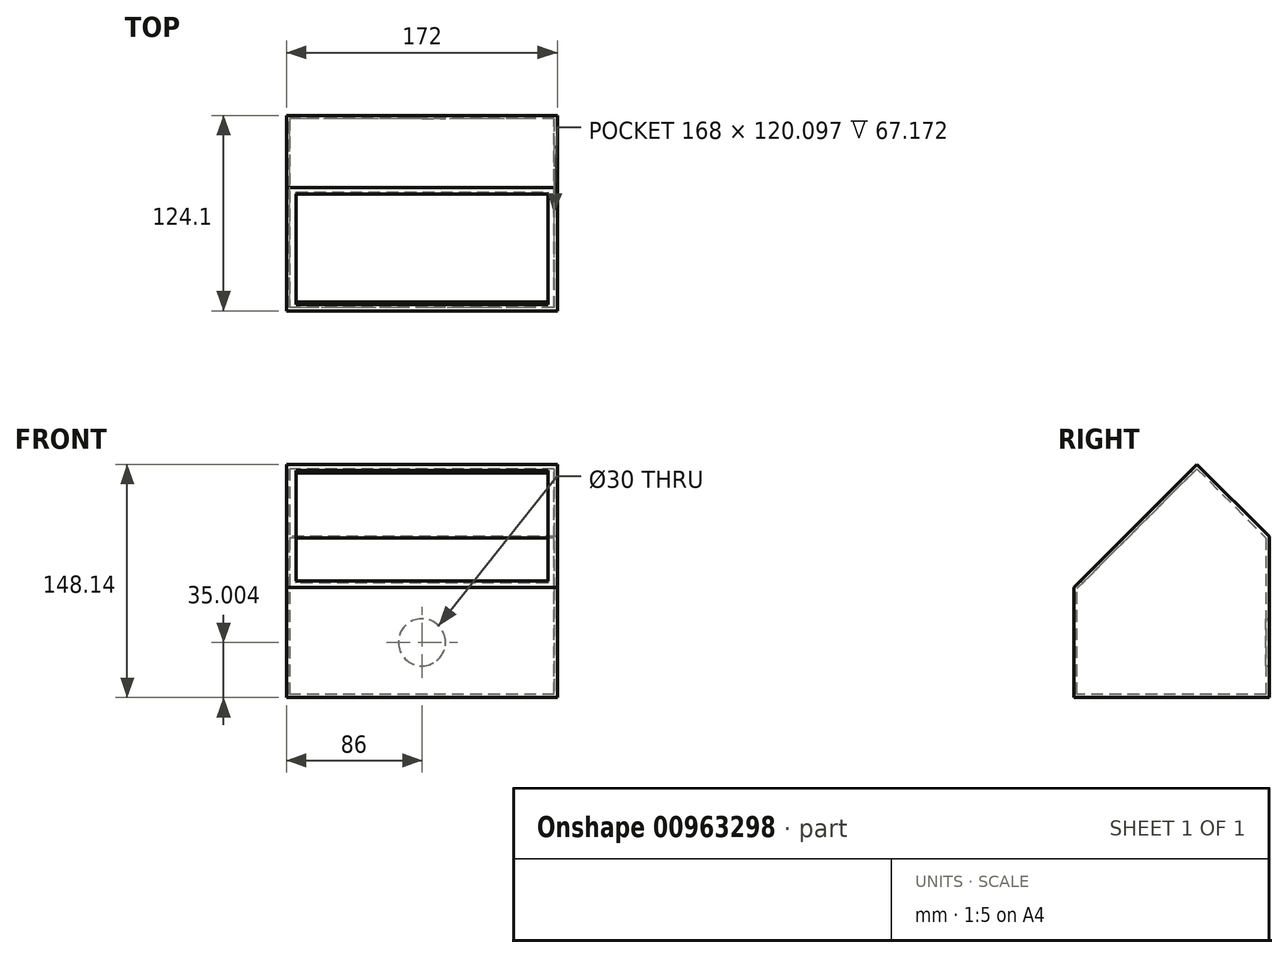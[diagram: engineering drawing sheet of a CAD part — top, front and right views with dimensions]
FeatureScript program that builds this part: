
annotation { "Feature Type Name" : "Feature", "Feature Type Description" : "" }
export const myFeature = defineFeature(function(context is Context, id is Id, definition is map)
    precondition{}
    {
        {
            var Q0;
            Q0=qCreatedBy(makeId("Right.planeOp"),FACE);
            var sketch = newSketch(context, id + "F0", { "sketchPlane" : qUnion([Q0])});
            skLineSegment(sketch, "E0", {"start": v(17.16, 48.46) * mm, "end": v(-60.98, -29.68) * mm});
            skLineSegment(sketch, "E1", {"start": v(63.12, 2.5) * mm, "end": v(17.16, 48.46) * mm});
            skLineSegment(sketch, "E2", {"start": v(-60.98, -29.68) * mm, "end": v(-60.98, -99.68) * mm});
            skLineSegment(sketch, "E3", {"start": v(-60.98, -99.68) * mm, "end": v(63.12, -99.68) * mm});
            skLineSegment(sketch, "E4", {"start": v(63.12, -99.68) * mm, "end": v(63.12, 2.5) * mm});
            skLineSegment(sketch, "E5.0", {"start": v(-58.98, -97.68) * mm, "end": v(61.12, -97.68) * mm});
            skLineSegment(sketch, "E5.1", {"start": v(-58.98, -30.5) * mm, "end": v(-58.98, -97.68) * mm});
            skLineSegment(sketch, "E5.2", {"start": v(61.12, -97.68) * mm, "end": v(61.12, 1.67) * mm});
            skLineSegment(sketch, "E5.3", {"start": v(61.12, 1.67) * mm, "end": v(17.16, 45.63) * mm});
            skLineSegment(sketch, "E5.4", {"start": v(17.16, 45.63) * mm, "end": v(-58.98, -30.5) * mm});
            skSolve(sketch);
        }
        {
            var Q0;
            Q0=makeQuery(id+"F0.imprint","IMPRINT",FACE,{"disambiguationData":[TD([[makeQuery(id+"F0.imprint","IMPRINT",EDGE,{"derivedFrom":sQuery(id+"F0.wireOp",EDGE,"E0")}),1.0]])]});
            extrude(context, id + "F1", {"entities" : qUnion([Q0]), "endBound" : BoundingType.SYMMETRIC, "depth" : 172 * mm, "offsetDistance" : 25 * mm});
        }
        {
            var Q0;
            Q0=makeQuery(id+"F1.opExtrude","SWEPT_FACE",FACE,{"disambiguationData":[OSD([sQuery(id+"F0.wireOp",EDGE,"E0")])]});
            var sketch = newSketch(context, id + "F2", { "sketchPlane" : qUnion([Q0])});
            skLineSegment(sketch, "E6.0", {"start": v(-80, 40.65) * mm, "end": v(-80, -58.35) * mm});
            skLineSegment(sketch, "E6.1", {"start": v(80, 40.65) * mm, "end": v(-80, 40.65) * mm});
            skLineSegment(sketch, "E6.2", {"start": v(80, -58.35) * mm, "end": v(80, 40.65) * mm});
            skLineSegment(sketch, "E6.3", {"start": v(-80, -58.35) * mm, "end": v(80, -58.35) * mm});
            skSolve(sketch);
        }
        {
            var Q0;
            Q0=makeQuery(id+"F2.imprint","IMPRINT",FACE,{"disambiguationData":[TD([[makeQuery(id+"F2.imprint","IMPRINT",EDGE,{"derivedFrom":sQuery(id+"F2.wireOp",EDGE,"E6.0")}),1.0]])]});
            extrude(context, id + "F3", {"entities" : qUnion([Q0]), "operationType" : NewBodyOperationType.REMOVE, "oppositeDirection" : true, "depth" : 25 * mm, "offsetDistance" : 25 * mm});
        }
        {
            var Q0;
            Q0=makeQuery(id+"F1.opExtrude","SWEPT_FACE",FACE,{"disambiguationData":[OSD([sQuery(id+"F0.wireOp",EDGE,"E4")])]});
            var sketch = newSketch(context, id + "F4", { "sketchPlane" : qUnion([Q0])});
            skCircle(sketch, "E7", {"center": v(0, -64.68) * mm, "radius": 15 * mm});
            skSolve(sketch);
        }
        {
            var Q0;
            Q0 = qSketchRegion(id + "F4", true);
            extrude(context, id + "F5", {"entities" : qUnion([Q0]), "operationType" : NewBodyOperationType.REMOVE, "oppositeDirection" : true, "depth" : 25 * mm, "offsetDistance" : 25 * mm});
        }
        {
            var Q0;
            Q0=makeQuery(id+"F1.opExtrude","CAP_FACE",FACE,{"disambiguationData":[OSD([sQuery(id+"F0.wireOp",EDGE,"E0"),sQuery(id+"F0.wireOp",EDGE,"E1"),sQuery(id+"F0.wireOp",EDGE,"E2"),sQuery(id+"F0.wireOp",EDGE,"E3"),sQuery(id+"F0.wireOp",EDGE,"E4"),sQuery(id+"F0.wireOp",EDGE,"E5.0"),sQuery(id+"F0.wireOp",EDGE,"E5.1"),sQuery(id+"F0.wireOp",EDGE,"E5.2"),sQuery(id+"F0.wireOp",EDGE,"E5.3"),sQuery(id+"F0.wireOp",EDGE,"E5.4")])],"isStart":false});
            var sketch = newSketch(context, id + "F6", { "sketchPlane" : qUnion([Q0])});
            skLineSegment(sketch, "E8", {"start": v(17.16, 48.46) * mm, "end": v(-60.98, -29.68) * mm});
            skLineSegment(sketch, "E9", {"start": v(-60.98, -29.68) * mm, "end": v(-60.98, -99.68) * mm});
            skLineSegment(sketch, "E10", {"start": v(-60.98, -99.68) * mm, "end": v(63.12, -99.68) * mm});
            skLineSegment(sketch, "E11", {"start": v(63.12, -99.68) * mm, "end": v(63.12, 2.5) * mm});
            skLineSegment(sketch, "E12", {"start": v(63.12, 2.5) * mm, "end": v(17.16, 48.46) * mm});
            skSolve(sketch);
        }
        {
            var Q0;
            Q0 = qSketchRegion(id + "F6", true);
            extrude(context, id + "F7", {"entities" : qUnion([Q0]), "operationType" : NewBodyOperationType.ADD, "oppositeDirection" : true, "depth" : 2 * mm, "offsetDistance" : 25 * mm});
        }
        {
            var Q0;
            Q0=makeQuery(id+"F1.opExtrude","CAP_FACE",FACE,{"disambiguationData":[OSD([sQuery(id+"F0.wireOp",EDGE,"E0"),sQuery(id+"F0.wireOp",EDGE,"E1"),sQuery(id+"F0.wireOp",EDGE,"E2"),sQuery(id+"F0.wireOp",EDGE,"E3"),sQuery(id+"F0.wireOp",EDGE,"E4"),sQuery(id+"F0.wireOp",EDGE,"E5.0"),sQuery(id+"F0.wireOp",EDGE,"E5.1"),sQuery(id+"F0.wireOp",EDGE,"E5.2"),sQuery(id+"F0.wireOp",EDGE,"E5.3"),sQuery(id+"F0.wireOp",EDGE,"E5.4")])],"isStart":true});
            var sketch = newSketch(context, id + "F8", { "sketchPlane" : qUnion([Q0])});
            skLineSegment(sketch, "E13", {"start": v(-63.12, 2.5) * mm, "end": v(-17.16, 48.46) * mm});
            skLineSegment(sketch, "E14", {"start": v(-17.16, 48.46) * mm, "end": v(60.98, -29.68) * mm});
            skLineSegment(sketch, "E15", {"start": v(60.98, -29.68) * mm, "end": v(60.98, -99.68) * mm});
            skLineSegment(sketch, "E16", {"start": v(60.98, -99.68) * mm, "end": v(-63.12, -99.68) * mm});
            skLineSegment(sketch, "E17", {"start": v(-63.12, -99.68) * mm, "end": v(-63.12, 2.5) * mm});
            skSolve(sketch);
        }
        {
            var Q0;
            Q0 = qSketchRegion(id + "F8", true);
            extrude(context, id + "F9", {"entities" : qUnion([Q0]), "operationType" : NewBodyOperationType.ADD, "oppositeDirection" : true, "depth" : 2 * mm, "offsetDistance" : 25 * mm});
        }
    });
